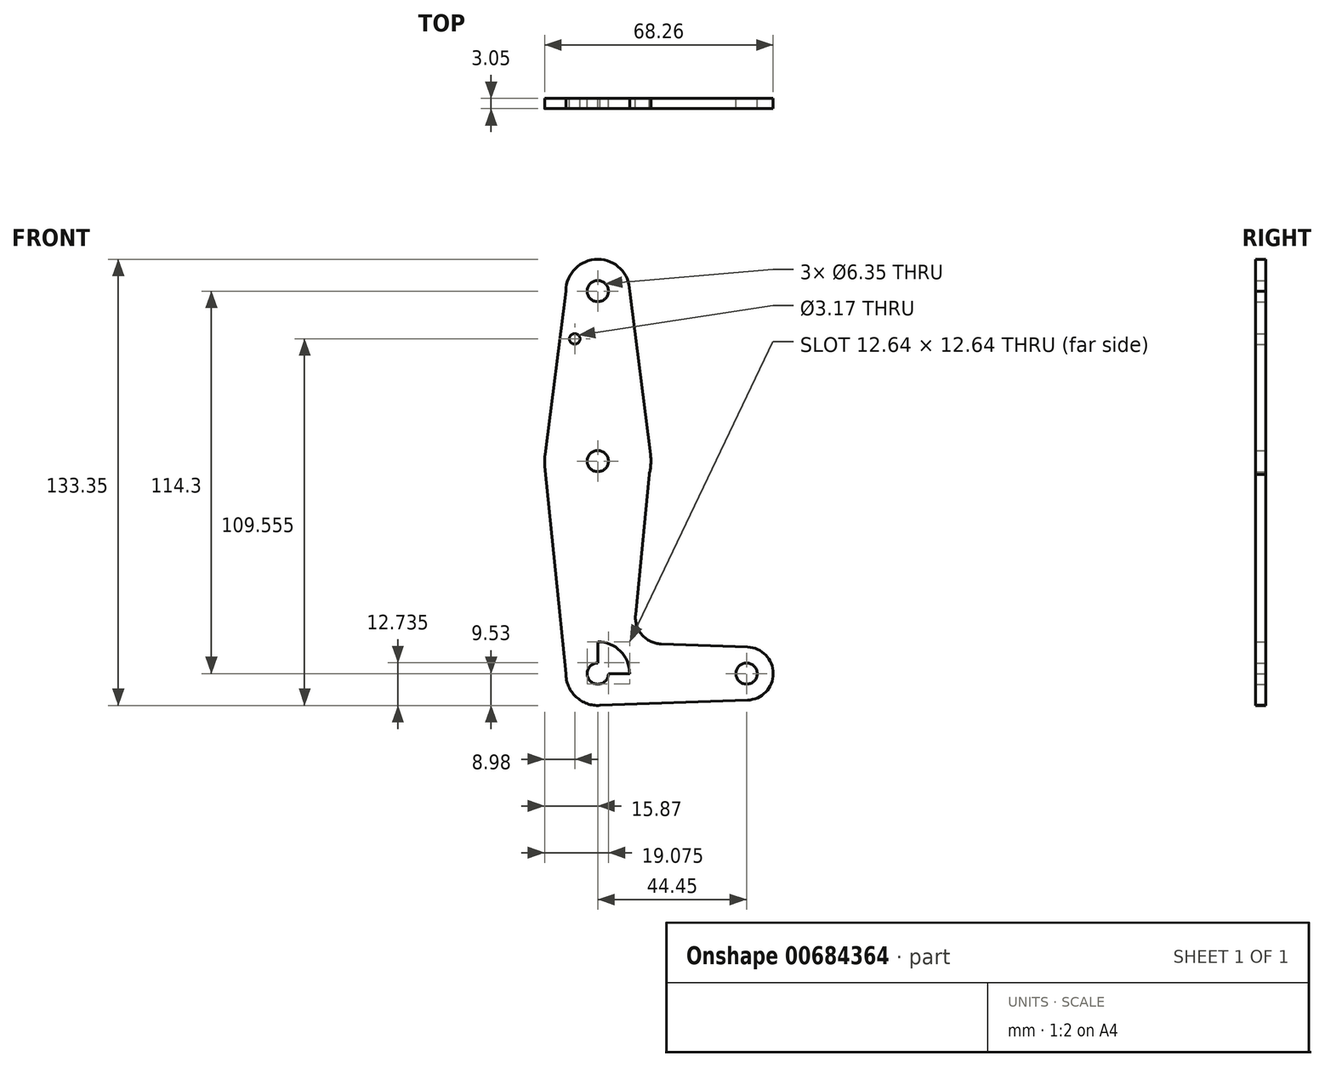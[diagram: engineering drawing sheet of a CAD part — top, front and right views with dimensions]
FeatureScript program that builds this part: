
annotation { "Feature Type Name" : "Feature", "Feature Type Description" : "" }
export const myFeature = defineFeature(function(context is Context, id is Id, definition is map)
    precondition{}
    {
        {
            var Q0;
            Q0=qCreatedBy(makeId("Front.planeOp"),FACE);
            var sketch = newSketch(context, id + "F0", { "sketchPlane" : qUnion([Q0])});
            skCircle(sketch, "E0", {"center": v(0, 0) * mm, "radius": 9.53 * mm});
            skLineSegment(sketch, "E1", {"start": v(0, 0) * mm, "end": v(0, 63.5) * mm});
            skCircle(sketch, "E2", {"center": v(0, 63.5) * mm, "radius": 15.88 * mm});
            skLineSegment(sketch, "E3", {"start": v(0, 0) * mm, "end": v(0, 114.3) * mm});
            skCircle(sketch, "E4", {"center": v(0, 114.3) * mm, "radius": 9.52 * mm});
            skLineSegment(sketch, "E5", {"start": v(0, 0) * mm, "end": v(44.45, 0) * mm});
            skCircle(sketch, "E6", {"center": v(44.45, 0) * mm, "radius": 7.94 * mm});
            skLineSegment(sketch, "E7", {"start": v(-9.52, 114.3) * mm, "end": v(-15.75, 65.5) * mm});
            skLineSegment(sketch, "E8", {"start": v(9.52, 114.3) * mm, "end": v(15.75, 65.5) * mm});
            skLineSegment(sketch, "E9", {"start": v(15.75, 63.5) * mm, "end": v(11.28, 17.57) * mm});
            skLineSegment(sketch, "E10", {"start": v(18.9, 8.85) * mm, "end": v(44.73, 7.93) * mm});
            skLineSegment(sketch, "E11", {"start": v(0, -9.53) * mm, "end": v(44.73, -7.93) * mm});
            skCircle(sketch, "E12", {"center": v(0, 114.3) * mm, "radius": 3.18 * mm});
            skCircle(sketch, "E13", {"center": v(0, 63.5) * mm, "radius": 3.18 * mm});
            skCircle(sketch, "E14", {"center": v(0, 0) * mm, "radius": 3.18 * mm});
            skCircle(sketch, "E15", {"center": v(44.45, 0) * mm, "radius": 3.18 * mm});
            skLineSegment(sketch, "E16", {"start": v(0, 63.5) * mm, "end": v(0, 100.03) * mm});
            skCircle(sketch, "E17", {"center": v(-6.89, 100.03) * mm, "radius": 1.59 * mm});
            skPoint(sketch, "E18.newPointB", {"position": v(9.57, 0) * mm});
            skArc(sketch, "E18.filletArc", {"start": v(11.28, 17.57) * mm, "mid": v(13.21, 11.56) * mm, "end": v(18.9, 8.85) * mm});
            skLineSegment(sketch, "E19", {"start": v(-9.53, 0) * mm, "end": v(-15.8, 61.9) * mm});
            skSolve(sketch);
        }
        {
            var Q0;
            Q0 = qSketchRegion(id + "F0", true);
            var Q1;
            {var subQ0=sQuery(id+"F0.wireOp",EDGE,"E3");var subQ1=sQuery(id+"F0.wireOp",EDGE,"E0");var subQ2=makeQuery(id+"F0.imprint","INTERSECT",VERTEX,{"derivedFrom":[subQ1,subQ0]});Q1=makeQuery(id+"F0.imprint","IMPRINT",FACE,{"disambiguationData":[TD([[makeQuery(id+"F0.imprint","IMPRINT",EDGE,{"disambiguationData":[TD([[subQ2,1.0]])],"derivedFrom":subQ1}),1.0]])]});}
            extrude(context, id + "F1", {"entities" : qUnion([Q0, Q1]), "depth" : 3.05 * mm, "offsetDistance" : 25.4 * mm});
        }
    });
